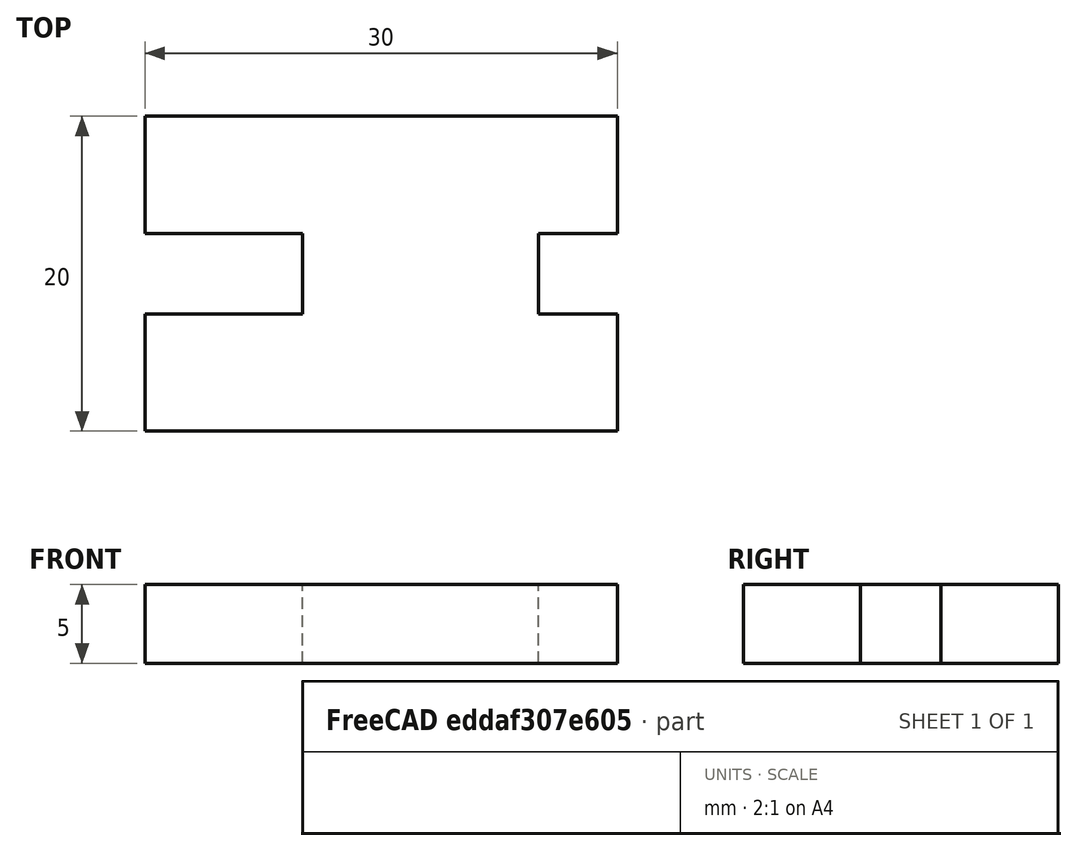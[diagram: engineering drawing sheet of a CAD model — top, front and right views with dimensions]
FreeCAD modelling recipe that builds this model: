
FCSTD DOCUMENT  (FreeCAD 1.0R39319 (Git))
Label: X Axis Near Leg Short Version
License: All rights reserved
LicenseURL: https://en.wikipedia.org/wiki/All_rights_reserved
objects: PartDesign::CoordinateSystem×2, Sketcher::SketchObject×1, PartDesign::Pad×1, PartDesign::Body×1, App::Part×1
note: 8 computed .brp shape members not serialized (recipe doc carries the construction recipe); baked Part::Feature solids carry a one-line shape summary decoded from their .brp

FEATURE [Sketcher::SketchObject] Sketch
  ArcFitTolerance = 1e-06
  AttachmentSupport = -> [XY_Plane001]
  FullyConstrained = true
  MakeInternals = false
  MapMode = 5
  sketch-geometry (14):
    g0: LineSegment StartX=0 StartY=2.55 StartZ=0 EndX=0 EndY=10 EndZ=0
    g1: LineSegment StartX=0 StartY=10 StartZ=0 EndX=30 EndY=10 EndZ=0
    g2: LineSegment StartX=30 StartY=10 StartZ=0 EndX=30 EndY=2.55 EndZ=0
    g3: LineSegment StartX=30 StartY=2.55 StartZ=0 EndX=25 EndY=2.55 EndZ=0
    g4: LineSegment StartX=25 StartY=2.55 StartZ=0 EndX=25 EndY=-2.55 EndZ=0
    g5: LineSegment StartX=25 StartY=-2.55 StartZ=0 EndX=30 EndY=-2.55 EndZ=0
    g6: LineSegment StartX=30 StartY=-2.55 StartZ=0 EndX=30 EndY=-10 EndZ=0
    g7: LineSegment StartX=30 StartY=-10 StartZ=0 EndX=0 EndY=-10 EndZ=0
    g8: LineSegment StartX=0 StartY=-10 StartZ=0 EndX=0 EndY=-2.55 EndZ=0
    g9: LineSegment StartX=0 StartY=-2.55 StartZ=0 EndX=10 EndY=-2.55 EndZ=0
    g10: LineSegment StartX=10 StartY=-2.55 StartZ=0 EndX=10 EndY=2.55 EndZ=0
    g11: LineSegment StartX=10 StartY=2.55 StartZ=0 EndX=0 EndY=2.55 EndZ=0
    g12: GeomPoint [constr] X=10 Y=0 Z=0
    g13: GeomPoint [constr] X=25 Y=2e-16 Z=0
  constraints (38):
    c: Coincident(g0,g1)
    c: Horizontal(g1)
    c: Coincident(g1,g2)
    c: Coincident(g2,g3)
    c: Horizontal(g3)
    c: Coincident(g3,g4)
    c: Vertical(g4)
    c: Coincident(g4,g5)
    c: Horizontal(g5)
    c: Coincident(g5,g6)
    c: Coincident(g6,g7)
    c: Horizontal(g7)
    c: Coincident(g7,g8)
    c: Coincident(g8,g9)
    c: Coincident(g9,g10)
    c: Coincident(g10,g11)
    c: Coincident(g11,g0)
    c: Vertical(g0)
    c: Horizontal(g11)
    c: Horizontal(g9)
    c: Vertical(g10)
    c: Vertical(g8)
    c: Vertical(g2)
    c: Vertical(g6)
    c: PointOnObject(g0,g8)
    c: PointOnObject(g5,g2)
    c: Symmetric(g10,g10,g12)
    c: Symmetric(g4,g4,g13)
    c: Distance(g9,g11) = 5.1
    c: DistanceY(g4,g4) = 5.1
    c: Distance(g7,g1) = 20
    c: Distance(g12,g1) = 10
    c: Distance(g13,g1) = 10
    c: DistanceX(g3,g3) = 5
    c: DistanceX(g11,g11) = 10
    c: PointOnObject(g12,g-1)
    c: PointOnObject(g8,g-2)
    c: DistanceX(g1,g1) = 30
FEATURE [PartDesign::Pad] Pad
  Direction = (0,0,1)
  Length = 5
  Length2 = 10
  Midplane = true
  Profile = -> Sketch
  ReferenceAxis = -> Sketch [N_Axis]
  Refine = true
  Suppressed = false
  Type = 0
FEATURE [PartDesign::Body] Body  label="X Axis Near Leg Short Version001"
  AllowCompound = false
  Group = -> [Sketch,Pad]
  Origin = -> Origin001
  Tip = -> Pad
FEATURE [PartDesign::CoordinateSystem] LCS_1
  AttacherType = Attacher::AttachEngine3D
  AttachmentOffset = pos=(10,0,0) rot=(0,0,1;0rad)
  AttachmentSupport = -> [XY_Plane001]
  MapMode = 2
  Placement = pos=(10,0,0) rot=(0,0,1;0rad)
FEATURE [PartDesign::CoordinateSystem] LCS_2
  AttacherType = Attacher::AttachEngine3D
  AttachmentOffset = pos=(25,0,0) rot=(0,0,1;0rad)
  AttachmentSupport = -> [XY_Plane001]
  MapMode = 2
  Placement = pos=(25,0,0) rot=(0,0,1;0rad)
FEATURE [App::Part] Part  label="X Axis Near Leg Short Version"
  Group = -> [Body,LCS_1,LCS_2]
  Origin = -> Origin
